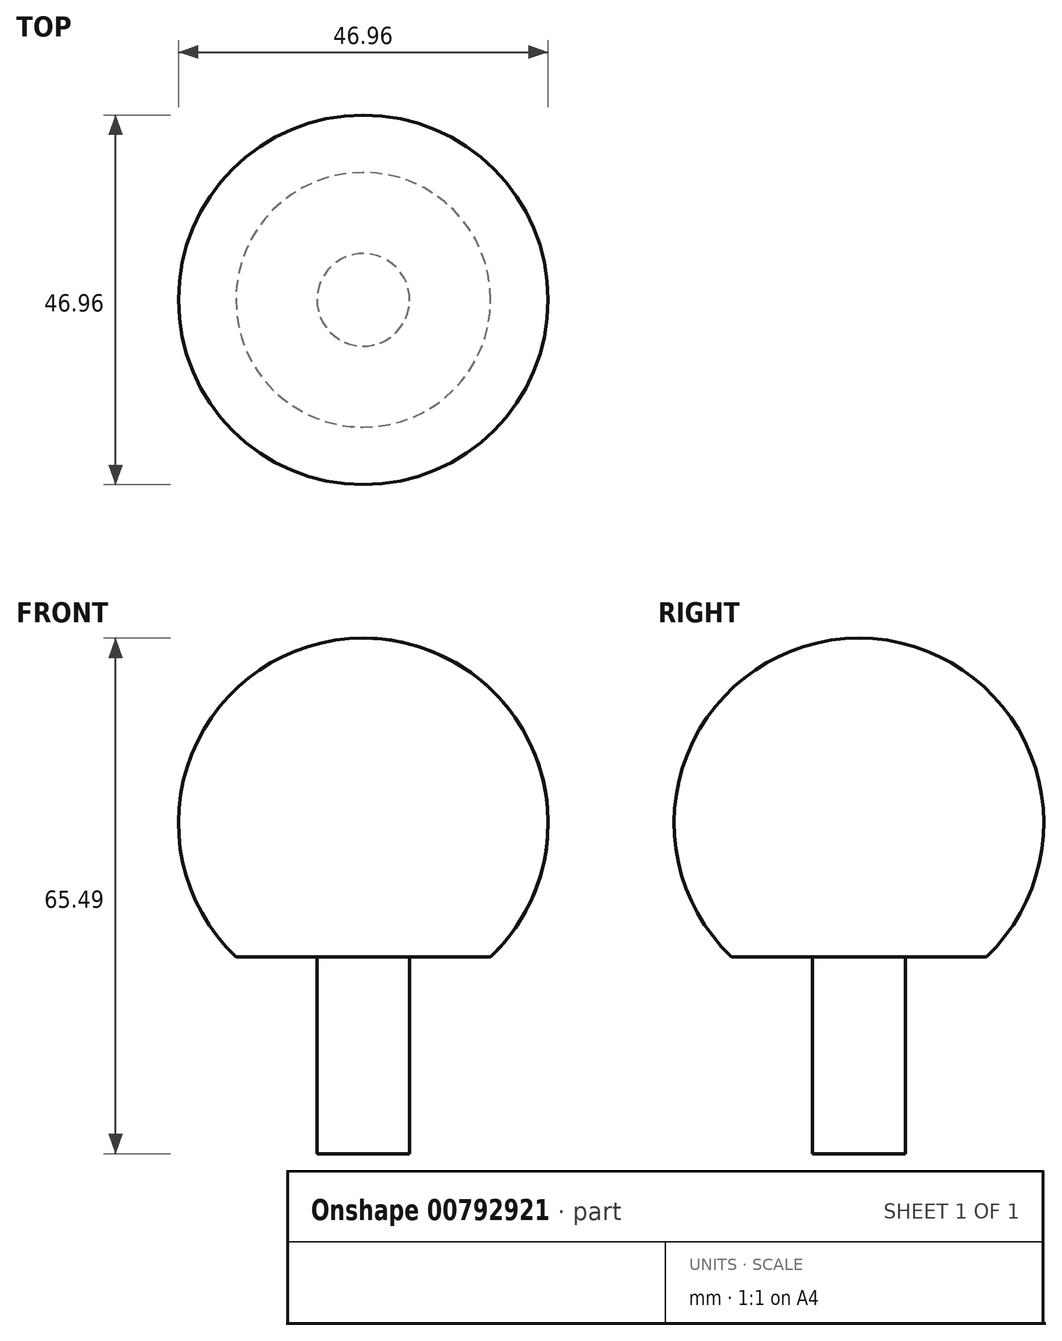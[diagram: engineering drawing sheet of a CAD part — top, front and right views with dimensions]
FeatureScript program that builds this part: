
annotation { "Feature Type Name" : "Feature", "Feature Type Description" : "" }
export const myFeature = defineFeature(function(context is Context, id is Id, definition is map)
    precondition{}
    {
        {
            var Q0;
            Q0=qCreatedBy(makeId("Front.planeOp"),FACE);
            var sketch = newSketch(context, id + "F0", { "sketchPlane" : qUnion([Q0])});
            skArc(sketch, "E0", {"start": v(0, 23.48) * mm, "mid": v(23.48, 0) * mm, "end": v(0, -23.48) * mm});
            skLineSegment(sketch, "E1", {"start": v(0, 23.48) * mm, "end": v(0, -23.48) * mm});
            skLineSegment(sketch, "E2", {"start": v(0, -17.01) * mm, "end": v(16.18, -17.01) * mm});
            skSolve(sketch);
        }
        {
            var Q0;
            {var subQ3=sQuery(id+"F0.wireOp",EDGE,"E2");Q0=makeQuery(id+"F0.imprint","IMPRINT",FACE,{"disambiguationData":[TD([[makeQuery(id+"F0.imprint","IMPRINT",EDGE,{"derivedFrom":subQ3}),1.0]])]});}
            var Q1;
            Q1=sQuery(id+"F0.wireOp",EDGE,"E1");
            revolve(context, id + "F1", {"surfaceOperationType" : NewSurfaceOperationType.NEW, "entities" : qUnion([Q0]), "axis" : qUnion([Q1]), "revolveType" : RevolveType.FULL});
        }
        {
            var Q0;
            Q0=makeQuery(id+"F1.opRevolve","SWEPT_FACE",FACE,{"disambiguationData":[OSD([sQuery(id+"F0.wireOp",EDGE,"E2")])]});
            var sketch = newSketch(context, id + "F2", { "sketchPlane" : qUnion([Q0])});
            skCircle(sketch, "E3", {"center": v(0, 0) * mm, "radius": 5.89 * mm});
            skSolve(sketch);
        }
        {
            var Q0;
            Q0 = qSketchRegion(id + "F2", true);
            extrude(context, id + "F3", {"entities" : qUnion([Q0]), "operationType" : NewBodyOperationType.ADD, "depth" : 25 * mm, "offsetDistance" : 25 * mm});
        }
    });
